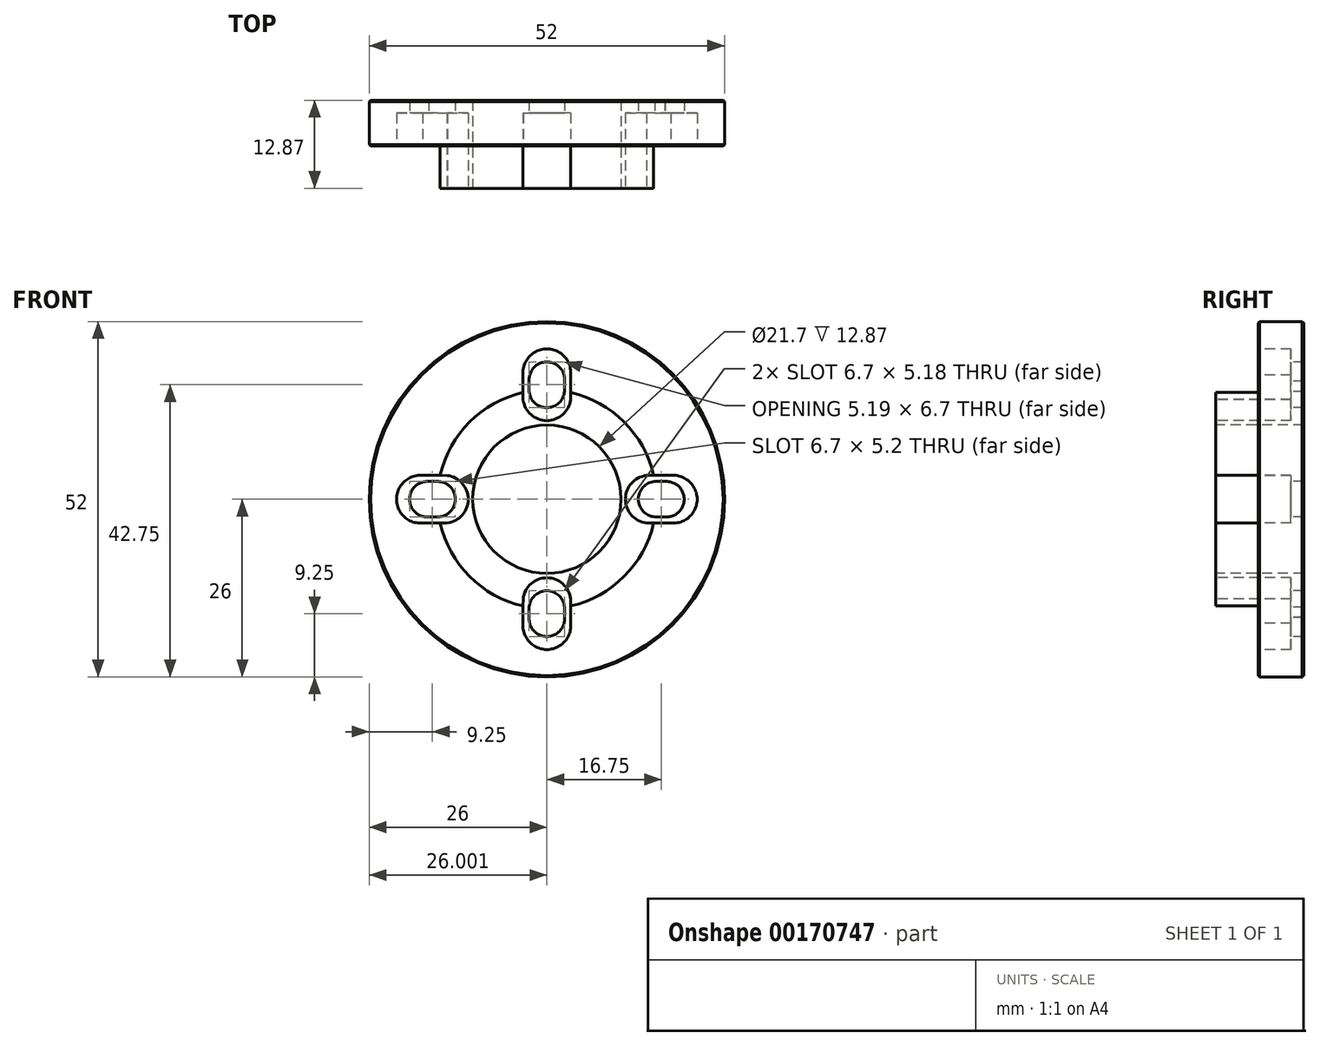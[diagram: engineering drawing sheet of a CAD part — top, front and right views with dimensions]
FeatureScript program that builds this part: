
annotation { "Feature Type Name" : "Feature", "Feature Type Description" : "" }
export const myFeature = defineFeature(function(context is Context, id is Id, definition is map)
    precondition{}
    {
        {
            var Q0;
            Q0=qCreatedBy(makeId("Front.planeOp"),FACE);
            var sketch = newSketch(context, id + "F0", { "sketchPlane" : qUnion([Q0])});
            skCircle(sketch, "E0", {"center": v(0, 0) * mm, "radius": 26 * mm});
            skCircle(sketch, "E1", {"center": v(0, 0) * mm, "radius": 17.5 * mm, "construction": true});
            skCircle(sketch, "E2", {"center": v(0, 0) * mm, "radius": 16 * mm, "construction": true});
            skLineSegment(sketch, "E3", {"start": v(-19.16, 0) * mm, "end": v(21.52, 0) * mm, "construction": true});
            skArc(sketch, "E4", {"start": v(-17.3, 2.6) * mm, "mid": v(-20.1, 0) * mm, "end": v(-17.3, -2.6) * mm});
            skLineSegment(sketch, "E5", {"start": v(0, 21.08) * mm, "end": v(0, -18.32) * mm, "construction": true});
            skCircle(sketch, "E6", {"center": v(0, 0) * mm, "radius": 10.85 * mm});
            skArc(sketch, "E7", {"start": v(-16.01, -2.6) * mm, "mid": v(-13.4, 0) * mm, "end": v(-16.01, 2.6) * mm});
            skLineSegment(sketch, "E8", {"start": v(-17.3, 2.6) * mm, "end": v(-16.01, 2.6) * mm});
            skLineSegment(sketch, "E9", {"start": v(-17.3, -2.6) * mm, "end": v(-16.01, -2.6) * mm});
            skArc(sketch, "E10", {"start": v(-2.6, 15.79) * mm, "mid": v(0.01, 13.4) * mm, "end": v(2.6, 15.82) * mm});
            skArc(sketch, "E11", {"start": v(15.79, 2.6) * mm, "mid": v(13.4, 0) * mm, "end": v(15.79, -2.6) * mm});
            skLineSegment(sketch, "E12.top", {"start": v(2.6, 15.79) * mm, "end": v(2.6, 15.79) * mm});
            skLineSegment(sketch, "E12.left", {"start": v(2.6, 17.3) * mm, "end": v(2.6, 15.79) * mm});
            skLineSegment(sketch, "E12.right", {"start": v(-2.6, 17.3) * mm, "end": v(-2.6, 15.79) * mm});
            skLineSegment(sketch, "E13.bottom", {"start": v(17.3, 2.6) * mm, "end": v(15.79, 2.6) * mm});
            skLineSegment(sketch, "E13.top", {"start": v(17.27, -2.6) * mm, "end": v(15.79, -2.6) * mm});
            skLineSegment(sketch, "E13.right", {"start": v(15.79, 2.6) * mm, "end": v(15.79, 2.6) * mm});
            skLineSegment(sketch, "E14.left", {"start": v(2.6, -15.79) * mm, "end": v(2.6, -17.3) * mm});
            skLineSegment(sketch, "E14.right", {"start": v(-2.6, -15.79) * mm, "end": v(-2.6, -17.3) * mm});
            skArc(sketch, "E15.trimOffspring", {"start": v(17.27, -2.6) * mm, "mid": v(20.1, -0.02) * mm, "end": v(17.3, 2.6) * mm});
            skArc(sketch, "E16.trimOffspring", {"start": v(2.6, 17.3) * mm, "mid": v(0, 20.1) * mm, "end": v(-2.6, 17.3) * mm});
            skArc(sketch, "E17.trimOffspring", {"start": v(-2.6, -17.28) * mm, "mid": v(0, -20.1) * mm, "end": v(2.6, -17.3) * mm});
            skArc(sketch, "E18.trimOffspring", {"start": v(2.6, -15.79) * mm, "mid": v(0, -13.4) * mm, "end": v(-2.6, -15.79) * mm});
            skSolve(sketch);
        }
        {
            var Q0;
            Q0=qSketchRegion(id+"F0",true);
            extrude(context, id + "F1", {"entities" : qUnion([Q0]), "oppositeDirection" : true, "depth" : 6.67 * mm});
        }
        {
            var Q0;
            Q0=makeQuery(id+"F1.opExtrude","CAP_EDGE",EDGE,{"disambiguationData":[OSD([sQuery(id+"F0.wireOp",EDGE,"E0")])],"isStart":false});
            var Q1;
            Q1=makeQuery(id+"F1.opExtrude","CAP_EDGE",EDGE,{"disambiguationData":[OSD([sQuery(id+"F0.wireOp",EDGE,"E0")])],"isStart":true});
            chamfer(context, id + "F2", {"entities" : qUnion([Q0, Q1]), "width" : 0.2 * mm, "tangentPropagation" : true});
        }
        {
            var Q0;
            Q0=makeQuery(id+"F1.opExtrude","CAP_FACE",FACE,{"disambiguationData":[OSD([sQuery(id+"F0.wireOp",EDGE,"E0"),sQuery(id+"F0.wireOp",EDGE,"E2"),sQuery(id+"F0.wireOp",EDGE,"E4"),sQuery(id+"F0.wireOp",EDGE,"89fb1a86-b0a4-4fbc-8635-11969420c582.1.0")])],"isStart":true});
            var sketch = newSketch(context, id + "F3", { "sketchPlane" : qUnion([Q0])});
            skCircle(sketch, "E19", {"center": v(0, 0) * mm, "radius": 16 * mm});
            skSolve(sketch);
        }
        {
            var Q0;
            Q0=qSketchRegion(id+"F3",true);
            extrude(context, id + "F4", {"entities" : qUnion([Q0]), "operationType" : NewBodyOperationType.ADD, "depth" : (10.7 - 4.5) * mm});
        }
        {
            var Q0;
            Q0=makeQuery(id+"F4.opExtrude","CAP_FACE",FACE,{"disambiguationData":[OSD([sQuery(id+"F3.wireOp",EDGE,"E19")])],"isStart":false});
            var sketch = newSketch(context, id + "F5", { "sketchPlane" : qUnion([Q0])});
            skCircle(sketch, "E20", {"center": v(0, 0) * mm, "radius": 10.85 * mm});
            skCircle(sketch, "E21", {"center": v(0, 0) * mm, "radius": 15 * mm, "construction": true});
            skCircle(sketch, "E22", {"center": v(0, 0) * mm, "radius": 18.5 * mm, "construction": true});
            skArc(sketch, "E23", {"start": v(3.48, 18.16) * mm, "mid": v(0, 22) * mm, "end": v(-3.48, 18.16) * mm});
            skLineSegment(sketch, "E24", {"start": v(-3.48, 18.16) * mm, "end": v(-3.48, 14.6) * mm});
            skLineSegment(sketch, "E25", {"start": v(3.48, 18.16) * mm, "end": v(3.47, 14.57) * mm});
            skArc(sketch, "E26.trimOffspring", {"start": v(-3.48, 14.6) * mm, "mid": v(0, 11.5) * mm, "end": v(3.48, 14.6) * mm});
            skArc(sketch, "E27.1.0", {"start": v(-18.16, 3.48) * mm, "mid": v(-22, 0) * mm, "end": v(-18.16, -3.48) * mm});
            skLineSegment(sketch, "E27.1.1", {"start": v(-18.16, -3.48) * mm, "end": v(-14.6, -3.48) * mm});
            skArc(sketch, "E27.1.2", {"start": v(-14.6, -3.48) * mm, "mid": v(-11.5, 0) * mm, "end": v(-14.6, 3.48) * mm});
            skLineSegment(sketch, "E27.1.3", {"start": v(-18.16, 3.48) * mm, "end": v(-14.57, 3.47) * mm});
            skArc(sketch, "E27.2.0", {"start": v(-3.48, -18.16) * mm, "mid": v(0, -22) * mm, "end": v(3.48, -18.16) * mm});
            skLineSegment(sketch, "E27.2.1", {"start": v(3.48, -18.16) * mm, "end": v(3.48, -14.6) * mm});
            skArc(sketch, "E27.2.2", {"start": v(3.48, -14.6) * mm, "mid": v(0, -11.5) * mm, "end": v(-3.48, -14.6) * mm});
            skLineSegment(sketch, "E27.2.3", {"start": v(-3.48, -18.16) * mm, "end": v(-3.47, -14.57) * mm});
            skArc(sketch, "E27.3.0", {"start": v(18.16, -3.48) * mm, "mid": v(22, 0) * mm, "end": v(18.16, 3.48) * mm});
            skLineSegment(sketch, "E27.3.1", {"start": v(18.16, 3.48) * mm, "end": v(14.6, 3.48) * mm});
            skArc(sketch, "E27.3.2", {"start": v(14.6, 3.48) * mm, "mid": v(11.5, 0) * mm, "end": v(14.6, -3.48) * mm});
            skLineSegment(sketch, "E27.3.3", {"start": v(18.16, -3.48) * mm, "end": v(14.57, -3.47) * mm});
            skSolve(sketch);
        }
        {
            var Q0;
            Q0 = qSketchRegion(id + "F5", true);
            extrude(context, id + "F6", {"entities" : qUnion([Q0]), "operationType" : NewBodyOperationType.REMOVE, "oppositeDirection" : true, "depth" : 11 * mm});
        }
    });
